# Revit family: Pavilion_conference_table_AV24
name_source: partatom
category: Furniture
revit_build: Autodesk Revit 2017 (Build: 20171027_0315(x64)
units: mm (PartAtom-declared; Revit-internal decimal feet)

## family parameters
Always vertical = Yes
Cut with Voids When Loaded = No
OmniClass Number = 23.40.20.00
OmniClass Title = General Furniture and Specialties
Room Calculation Point = No
Shared = No
Work Plane-Based = No

## types (1)
- Pavilion_conference_table_AV24
    Base = &tradition Powder Coated Metal black matt
    Depth = 250cm / 98.4in
    Description = An expansion on the Pavilion dining table, this conference table features a longer and wider tabletop to cater to the contract market. Maintaining the original light and lyrical aesthetic of previous pieces, the conference table showcases a wooden veneer tabletop and stretcher, and a chrome or powder coated metal base.
    Design = Anderssen & Voll
    Design Year = 2022
    Gliders = &tradition Plastic Black Matt
    Height = 73cm / 28.7in
    Manufacturer = &Tradition
    Model = Pavilion conference table AV24
    Packaging dimensions & weight = Please see product fact sheet available from download page on website
    Stretcher = &tradition Lacquered Oak Black Matt Vertical
    Table Top = &tradition Lacquered Oak Black Matt Horizontal
    Type Comments = Pavilion
    URL = https://www.andtradition.com
    Variation = Please visit our website to see available colours and finishes.
    Width = 110cm / 43.3in

## geometry (parser evidence)
native form markers: Sweep x3
no freeform markers — native parametric forms only
